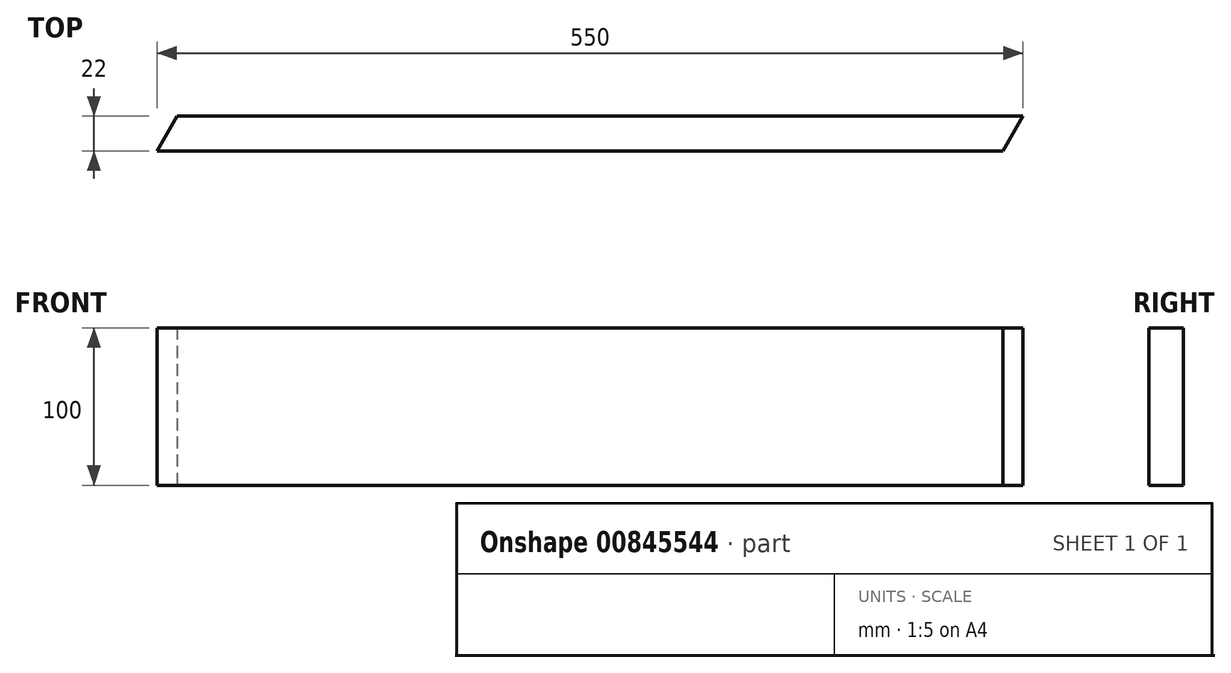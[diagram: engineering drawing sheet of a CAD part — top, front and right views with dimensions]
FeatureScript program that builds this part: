
annotation { "Feature Type Name" : "Feature", "Feature Type Description" : "" }
export const myFeature = defineFeature(function(context is Context, id is Id, definition is map)
    precondition{}
    {
        {
            var Q0;
            Q0=qCreatedBy(makeId("Top.planeOp"),FACE);
            var sketch = newSketch(context, id + "F0", { "sketchPlane" : qUnion([Q0])});
            skLineSegment(sketch, "E0.bottom", {"start": v(-262.3, 11) * mm, "end": v(275, 11) * mm});
            skLineSegment(sketch, "E0.top", {"start": v(-275, -11) * mm, "end": v(262.3, -11) * mm});
            skPoint(sketch, "E0.middle", {"position": v(0, 0) * mm});
            skLineSegment(sketch, "E1", {"start": v(-275, -11) * mm, "end": v(-262.3, 11) * mm});
            skPoint(sketch, "E0.left.start.orphan", {"position": v(-275, 11) * mm});
            skLineSegment(sketch, "E2", {"start": v(275, 11) * mm, "end": v(262.3, -11) * mm});
            skPoint(sketch, "E0.right.end.orphan", {"position": v(275, -11) * mm});
            skSolve(sketch);
        }
        {
            var Q0;
            Q0 = qSketchRegion(id + "F0", true);
            extrude(context, id + "F1", {"entities" : qUnion([Q0]), "depth" : 100 * mm, "offsetDistance" : 25 * mm});
        }
    });
